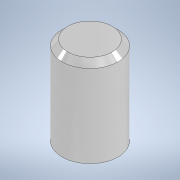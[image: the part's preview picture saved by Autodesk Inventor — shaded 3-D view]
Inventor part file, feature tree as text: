
AUTODESK INVENTOR PART (.ipt)
format: ipt  version: 2022 (Build 260153000, 153)  size: 99,328 bytes
history: native  units: in
note: dims shown in document units (in); Inventor stores cm internally (conversion verified against a paired STEP export)
features: extrude x1, chamfer x1, sketch x1
ambient origin geometry x8: Origin, YZ Plane, XZ Plane, XY Plane, X Axis, Y Axis, Z Axis, Center Point
bodies: Solid1 (feature_tree)
feature tree (3):
  extrude  "Extrusion1"  Depth=0.242in TaperAngle=0.0deg
  chamfer  "Chamfer1"  Distance=0.0157in Angle=45.0deg
  sketch  "Sketch1"  dims[d0=0.1535in d1=0.242in d2=0.0in d3=0.0157in d4=0.0787in d5=45.0deg]
